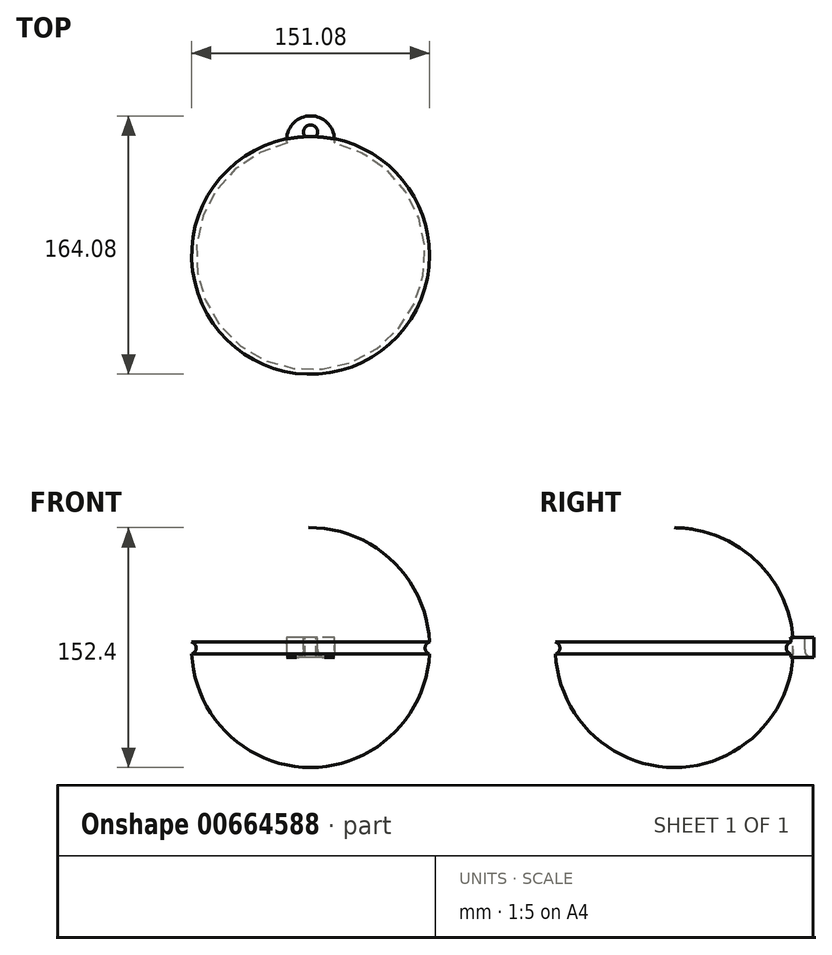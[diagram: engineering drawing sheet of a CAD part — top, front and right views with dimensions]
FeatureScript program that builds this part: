
annotation { "Feature Type Name" : "Feature", "Feature Type Description" : "" }
export const myFeature = defineFeature(function(context is Context, id is Id, definition is map)
    precondition{}
    {
        {
            var Q0;
            Q0=qCreatedBy(makeId("Front.planeOp"),FACE);
            var sketch = newSketch(context, id + "F0", { "sketchPlane" : qUnion([Q0])});
            skLineSegment(sketch, "E0", {"start": v(0, 0) * mm, "end": v(0, 152.4) * mm});
            skArc(sketch, "E1", {"start": v(0, 0) * mm, "mid": v(75.63, 76.2) * mm, "end": v(0, 152.4) * mm});
            skSolve(sketch);
        }
        {
            var Q0;
            Q0 = qSketchRegion(id + "F0", true);
            var Q1;
            Q1=sQuery(id+"F0.wireOp",EDGE,"E0");
            revolve(context, id + "F1", {"entities" : qUnion([Q0]), "axis" : qUnion([Q1]), "revolveType" : RevolveType.FULL});
        }
        {
            var Q0;
            Q0=qCreatedBy(makeId("Top.planeOp"),FACE);
            cPlane(context, id + "F2", {"entities" : qUnion([Q0]), "cplaneType" : CPlaneType.OFFSET, "offset" : 76.2 * mm, "width" : 152.4 * mm, "height" : 152.4 * mm});
        }
        {
            var Q0;
            Q0=qCreatedBy(id+"F2.planeOp",FACE);
            var sketch = newSketch(context, id + "F3", { "sketchPlane" : qUnion([Q0])});
            skCircle(sketch, "E2", {"center": v(0, 0) * mm, "radius": 75.66 * mm});
            skSolve(sketch);
        }
        {
            var Q0;
            Q0=qCreatedBy(makeId("Right.planeOp"),FACE);
            var sketch = newSketch(context, id + "F4", { "sketchPlane" : qUnion([Q0])});
            skCircle(sketch, "E3", {"center": v(76.7, 75.96) * mm, "radius": 3.98 * mm});
            skSolve(sketch);
        }
        {
            var Q0;
            Q0=makeQuery(id+"F4.imprint","IMPRINT",FACE,{"disambiguationData":[TD([[makeQuery(id+"F4.imprint","IMPRINT",EDGE,{"derivedFrom":sQuery(id+"F4.wireOp",EDGE,"E3")}),1.0]])]});
            var Q1;
            Q1=sQuery(id+"F3.wireOp",EDGE,"E2");
            sweep(context, id + "F5", {"operationType" : NewBodyOperationType.REMOVE, "profiles" : qUnion([Q0]), "path" : qUnion([Q1])});
        }
        {
            var Q0;
            Q0=qCreatedBy(makeId("Top.planeOp"),FACE);
            var sketch = newSketch(context, id + "F6", { "sketchPlane" : qUnion([Q0])});
            skEllipse(sketch, "E4", {"center": v(0, 0) * mm, "majorRadius": 84.27 * mm, "minorRadius": 29.45 * mm, "majorAxis": v(0, -1)});
            skSolve(sketch);
        }
        {
            var Q0;
            Q0=qCreatedBy(id+"F2.planeOp",FACE);
            var sketch = newSketch(context, id + "F7", { "sketchPlane" : qUnion([Q0])});
            skCircle(sketch, "E5", {"center": v(0, 73.37) * mm, "radius": 15.17 * mm});
            skSolve(sketch);
        }
        {
            var Q0;
            Q0 = qSketchRegion(id + "F7", true);
            extrude(context, id + "F8", {"entities" : qUnion([Q0]), "operationType" : NewBodyOperationType.ADD, "endBound" : BoundingType.SYMMETRIC, "depth" : 12.7 * mm, "offsetDistance" : 25.4 * mm});
        }
        {
            var Q0;
            Q0=makeQuery(id+"F8.opExtrude","CAP_FACE",FACE,{"disambiguationData":[OSD([sQuery(id+"F7.wireOp",EDGE,"E5")])],"isStart":false});
            var sketch = newSketch(context, id + "F9", { "sketchPlane" : qUnion([Q0])});
            skCircle(sketch, "E6", {"center": v(0, 78.27) * mm, "radius": 4.5 * mm});
            skPoint(sketch, "E6.centerSnap0", {"position": v(0, 75.36) * mm});
            skSolve(sketch);
        }
        {
            var Q0;
            {var subQ0=sQuery(id+"F9.wireOp",EDGE,"E6");var subQ1=makeQuery(id+"F8.boolean.opBoolean","INTERSECT",EDGE,{"derivedFrom":[makeQuery(id+"F5.boolean.opBoolean","SPLIT",FACE,{"disambiguationData":[OD(1.0)],"derivedFrom":makeQuery(id+"F1.opRevolve","SWEPT_FACE",FACE,{"disambiguationData":[OSD([sQuery(id+"F0.wireOp",EDGE,"E1")])]})}),makeQuery(id+"F8.opExtrude","CAP_FACE",FACE,{"disambiguationData":[OSD([sQuery(id+"F7.wireOp",EDGE,"E5")])],"isStart":false})]});var subQ2=makeQuery(id+"F9.imprint","INTERSECT",VERTEX,{"disambiguationData":[OD(0.0)],"derivedFrom":[subQ1,subQ0]});Q0=makeQuery(id+"F9.imprint","IMPRINT",FACE,{"disambiguationData":[TD([[makeQuery(id+"F9.imprint","IMPRINT",EDGE,{"disambiguationData":[TD([[subQ2,1.0]])],"derivedFrom":subQ0}),1.0]])]});}
            var Q1;
            Q1=sQuery(id+"F9.wireOp",EDGE,"E6");
            extrude(context, id + "F10", {"entities" : qUnion([Q0]), "operationType" : NewBodyOperationType.REMOVE, "surfaceEntities" : qUnion([Q1]), "endBound" : BoundingType.THROUGH_ALL, "oppositeDirection" : true, "depth" : 25.4 * mm, "offsetDistance" : 25.4 * mm});
        }
        {
            var Q0;
            Q0=makeQuery(id+"F10.boolean.opBoolean","COPY",EDGE,{"derivedFrom":makeQuery(id+"F10.opExtrude","CAP_EDGE",EDGE,{"disambiguationData":[OSD([sQuery(id+"F9.wireOp",EDGE,"E6")])],"isStart":true})});
            var Q1;
            Q1=makeQuery(id+"F10.boolean.opBoolean","INTERSECT",EDGE,{"derivedFrom":[makeQuery(id+"F8.opExtrude","CAP_FACE",FACE,{"disambiguationData":[OSD([sQuery(id+"F7.wireOp",EDGE,"E5")])],"isStart":true}),makeQuery(id+"F10.opExtrude","SWEPT_FACE",FACE,{"disambiguationData":[OSD([sQuery(id+"F9.wireOp",EDGE,"E6")])]})]});
            fillet(context, id + "F11", {"entities" : qUnion([Q0, Q1]), "radius" : 5.08 * mm, "tangentPropagation" : true, "allowEdgeOverflow" : false});
        }
    });
